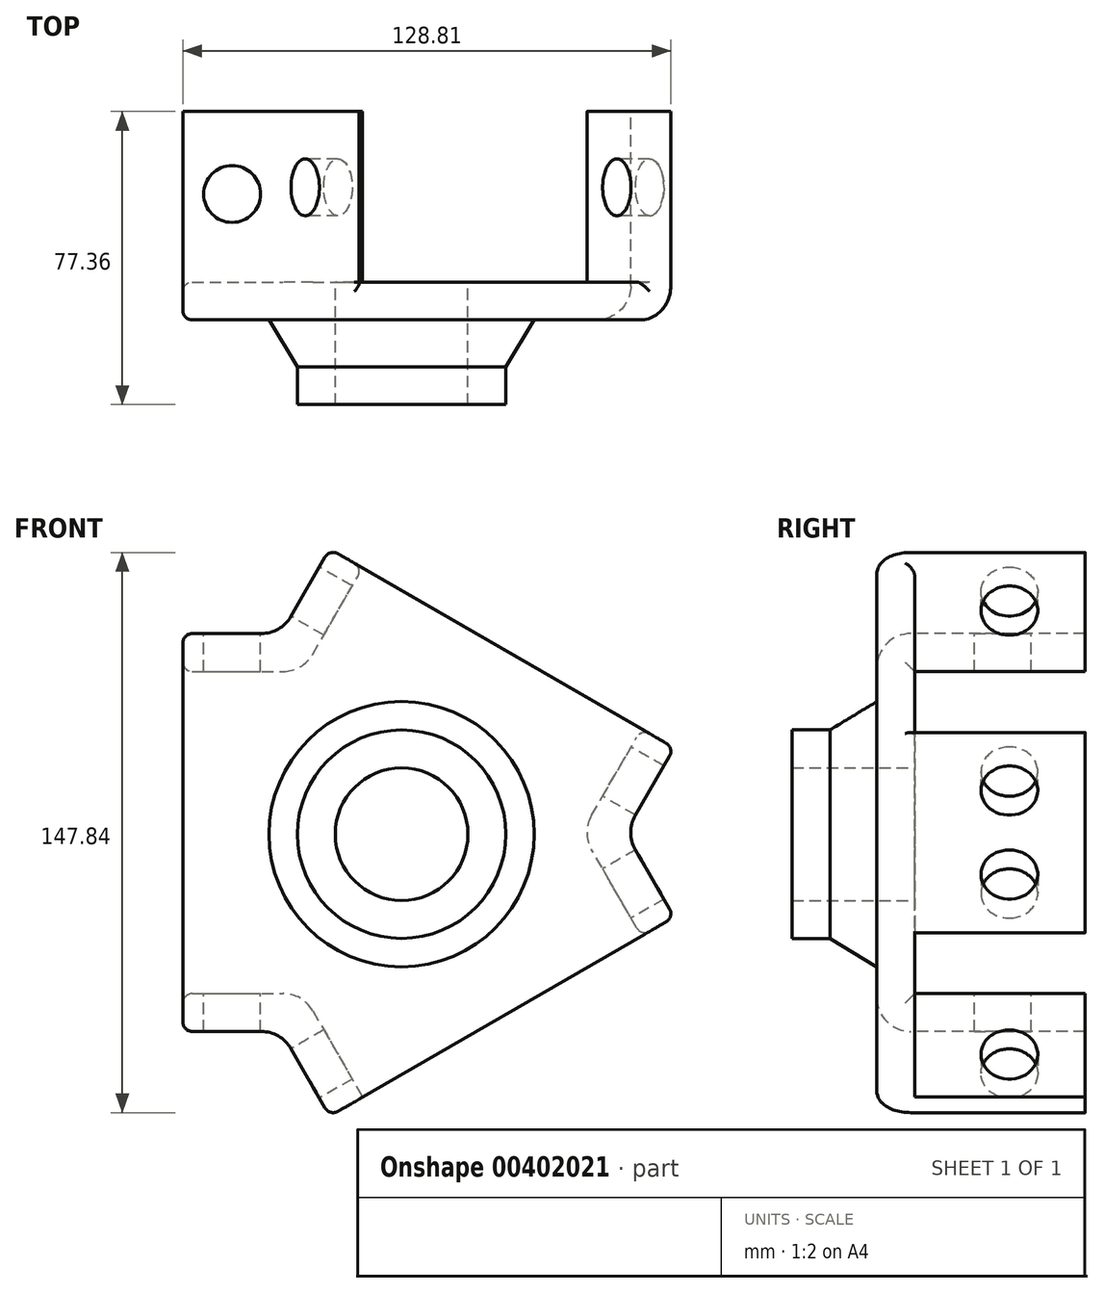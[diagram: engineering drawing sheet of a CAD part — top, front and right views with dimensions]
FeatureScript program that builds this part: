
annotation { "Feature Type Name" : "Feature", "Feature Type Description" : "" }
export const myFeature = defineFeature(function(context is Context, id is Id, definition is map)
    precondition{}
    {
        {
            var Q0;
            Q0=qCreatedBy(makeId("Front.planeOp"),FACE);
            var sketch = newSketch(context, id + "F0", { "sketchPlane" : qUnion([Q0])});
            skLineSegment(sketch, "E0", {"start": v(-84.9, 78.92) * mm, "end": v(-84.9, -26.08) * mm});
            skLineSegment(sketch, "E1", {"start": v(-84.9, 78.92) * mm, "end": v(-59, 78.92) * mm});
            skLineSegment(sketch, "E2", {"start": v(-59, 78.92) * mm, "end": v(-46.11, 101.26) * mm});
            skLineSegment(sketch, "E3", {"start": v(-46.11, 101.26) * mm, "end": v(44.82, 48.76) * mm});
            skLineSegment(sketch, "E4", {"start": v(44.82, 48.76) * mm, "end": v(31.92, 26.42) * mm});
            skLineSegment(sketch, "E5", {"start": v(31.92, 26.42) * mm, "end": v(44.82, 4.09) * mm});
            skLineSegment(sketch, "E6", {"start": v(44.82, 4.09) * mm, "end": v(-46.11, -48.41) * mm});
            skLineSegment(sketch, "E7", {"start": v(-46.11, -48.41) * mm, "end": v(-59, -26.08) * mm});
            skLineSegment(sketch, "E8", {"start": v(-84.9, -26.08) * mm, "end": v(-59, -26.08) * mm});
            skSolve(sketch);
        }
        {
            var Q0;
            Q0=makeQuery(id+"F0.imprint","IMPRINT",FACE,{"disambiguationData":[TD([[makeQuery(id+"F0.imprint","IMPRINT",EDGE,{"derivedFrom":sQuery(id+"F0.wireOp",EDGE,"E0")}),1.0]])]});
            extrude(context, id + "F1", {"entities" : qUnion([Q0]), "oppositeDirection" : true, "depth" : 10 * mm});
        }
        {
            var Q0;
            Q0=makeQuery(id+"F1.opExtrude","CAP_FACE",FACE,{"disambiguationData":[OSD([sQuery(id+"F0.wireOp",EDGE,"E0"),sQuery(id+"F0.wireOp",EDGE,"E1"),sQuery(id+"F0.wireOp",EDGE,"E2"),sQuery(id+"F0.wireOp",EDGE,"E3"),sQuery(id+"F0.wireOp",EDGE,"E4"),sQuery(id+"F0.wireOp",EDGE,"E5"),sQuery(id+"F0.wireOp",EDGE,"E6"),sQuery(id+"F0.wireOp",EDGE,"E7"),sQuery(id+"F0.wireOp",EDGE,"E8")])],"isStart":true});
            var sketch = newSketch(context, id + "F2", { "sketchPlane" : qUnion([Q0])});
            skPoint(sketch, "E9.startSnap0", {"position": v(-0.65, 75) * mm});
            skPoint(sketch, "E10", {"position": v(-27.16, 25.99) * mm});
            skSolve(sketch);
        }
        {
            var Q0;
            Q0=sQuery(id+"F2.wireOp",VERTEX,"E10");
            var Q1;
            Q1=sQuery(id+"F0.wireOp",EDGE,"E6");
            cPlane(context, id + "F3", {"entities" : qUnion([Q0, Q1]), "cplaneType" : CPlaneType.LINE_POINT, "offset" : 25 * mm, "width" : 150 * mm, "height" : 150 * mm});
        }
        {
            var Q0;
            Q0=qCreatedBy(id+"F3.planeOp",FACE);
            var sketch = newSketch(context, id + "F4", { "sketchPlane" : qUnion([Q0])});
            skLineSegment(sketch, "E11", {"start": v(0, 36.09) * mm, "end": v(78.9, 36.09) * mm, "construction": true});
            skLineSegment(sketch, "E12", {"start": v(22.36, 18.59) * mm, "end": v(12.36, 18.59) * mm});
            skLineSegment(sketch, "E13", {"start": v(12.36, 18.59) * mm, "end": v(12.36, 8.59) * mm});
            skLineSegment(sketch, "E14", {"start": v(12.36, 8.59) * mm, "end": v(22.36, 8.59) * mm});
            skLineSegment(sketch, "E15", {"start": v(22.36, 8.59) * mm, "end": v(22.36, 18.59) * mm});
            skLineSegment(sketch, "E16", {"start": v(0, 36.09) * mm, "end": v(0, 1.09) * mm});
            skLineSegment(sketch, "E17", {"start": v(12.36, 8.59) * mm, "end": v(0, 1.09) * mm});
            skLineSegment(sketch, "E18", {"start": v(12.36, 18.59) * mm, "end": v(-0.14, 18.59) * mm});
            skSolve(sketch);
        }
        {
            var Q0;
            Q0=makeQuery(id+"F1.opExtrude","CAP_FACE",FACE,{"disambiguationData":[OSD([sQuery(id+"F0.wireOp",EDGE,"E0"),sQuery(id+"F0.wireOp",EDGE,"E1"),sQuery(id+"F0.wireOp",EDGE,"E2"),sQuery(id+"F0.wireOp",EDGE,"E3"),sQuery(id+"F0.wireOp",EDGE,"E4"),sQuery(id+"F0.wireOp",EDGE,"E5"),sQuery(id+"F0.wireOp",EDGE,"E6"),sQuery(id+"F0.wireOp",EDGE,"E7"),sQuery(id+"F0.wireOp",EDGE,"E8")])],"isStart":false});
            var sketch = newSketch(context, id + "F5", { "sketchPlane" : qUnion([Q0])});
            skLineSegment(sketch, "E19.0", {"start": v(46.11, -48.41) * mm, "end": v(59, -26.08) * mm});
            skLineSegment(sketch, "E20.0", {"start": v(84.9, -26.08) * mm, "end": v(59, -26.08) * mm});
            skLineSegment(sketch, "E21.0", {"start": v(84.9, 78.92) * mm, "end": v(59, 78.92) * mm});
            skLineSegment(sketch, "E22.0", {"start": v(59, 78.92) * mm, "end": v(46.11, 101.26) * mm});
            skLineSegment(sketch, "E23.0", {"start": v(-31.92, 26.42) * mm, "end": v(-44.82, 4.09) * mm});
            skLineSegment(sketch, "E24.0", {"start": v(-44.82, 48.76) * mm, "end": v(-31.92, 26.42) * mm});
            skLineSegment(sketch, "E25", {"start": v(84.9, -26.08) * mm, "end": v(84.9, -16.08) * mm});
            skLineSegment(sketch, "E26", {"start": v(84.9, -16.08) * mm, "end": v(53.24, -16.08) * mm});
            skLineSegment(sketch, "E27", {"start": v(53.24, -16.08) * mm, "end": v(37.45, -43.41) * mm});
            skLineSegment(sketch, "E28", {"start": v(-36.16, -0.91) * mm, "end": v(-20.38, 26.42) * mm});
            skLineSegment(sketch, "E29", {"start": v(-20.38, 26.42) * mm, "end": v(-36.16, 53.76) * mm});
            skLineSegment(sketch, "E30", {"start": v(84.9, 68.92) * mm, "end": v(53.24, 68.92) * mm});
            skLineSegment(sketch, "E31", {"start": v(53.24, 68.92) * mm, "end": v(37.45, 96.26) * mm});
            skSolve(sketch);
        }
        {
            var Q0;
            {var subQ0=sQuery(id+"F5.wireOp",EDGE,"E19.0");Q0=makeQuery(id+"F5.imprint","IMPRINT",FACE,{"disambiguationData":[TD([[makeQuery(id+"F5.imprint","IMPRINT",EDGE,{"derivedFrom":subQ0}),1.0]])]});}
            var Q1;
            {var subQ4=sQuery(id+"F5.wireOp",EDGE,"E23.0");Q1=makeQuery(id+"F5.imprint","IMPRINT",FACE,{"disambiguationData":[TD([[makeQuery(id+"F5.imprint","IMPRINT",EDGE,{"derivedFrom":subQ4}),1.0]])]});}
            var Q2;
            {var subQ3=sQuery(id+"F5.wireOp",EDGE,"E21.0");Q2=makeQuery(id+"F5.imprint","IMPRINT",FACE,{"disambiguationData":[TD([[makeQuery(id+"F5.imprint","IMPRINT",EDGE,{"derivedFrom":subQ3}),1.0]])]});}
            extrude(context, id + "F6", {"entities" : qUnion([Q0, Q1, Q2]), "operationType" : NewBodyOperationType.ADD, "depth" : 45 * mm});
        }
        {
            var Q0;
            Q0=makeQuery(id+"F4.imprint","IMPRINT",FACE,{"disambiguationData":[TD([[makeQuery(id+"F4.imprint","IMPRINT",EDGE,{"derivedFrom":sQuery(id+"F4.wireOp",EDGE,"E12")}),1.0]])]});
            var Q1;
            {var subQ0=sQuery(id+"F4.wireOp",EDGE,"E13");Q1=makeQuery(id+"F4.imprint","IMPRINT",FACE,{"disambiguationData":[TD([[makeQuery(id+"F4.imprint","IMPRINT",EDGE,{"derivedFrom":subQ0}),-1.0]])]});}
            var Q2;
            Q2=sQuery(id+"F4.wireOp",EDGE,"E11");
            revolve(context, id + "F7", {"operationType" : NewBodyOperationType.ADD, "entities" : qUnion([Q0, Q1]), "axis" : qUnion([Q2]), "revolveType" : RevolveType.FULL});
        }
        {
            var Q0;
            Q0=makeQuery(id+"F6.boolean.opBoolean","MERGE",FACE,{"derivedFrom":[makeQuery(id+"F1.opExtrude","SWEPT_FACE",FACE,{"disambiguationData":[OSD([sQuery(id+"F0.wireOp",EDGE,"E2")])]}),makeQuery(id+"F6.opExtrude","SWEPT_FACE",FACE,{"disambiguationData":[OSD([sQuery(id+"F5.wireOp",EDGE,"E22.0")])]})]});
            var sketch = newSketch(context, id + "F8", { "sketchPlane" : qUnion([Q0])});
            skCircle(sketch, "E32", {"center": v(-35, 51.63) * mm, "radius": 7.5 * mm});
            skSolve(sketch);
        }
        {
            var Q0;
            Q0=makeQuery(id+"F6.boolean.opBoolean","MERGE",FACE,{"derivedFrom":[makeQuery(id+"F1.opExtrude","SWEPT_FACE",FACE,{"disambiguationData":[OSD([sQuery(id+"F0.wireOp",EDGE,"E1")])]}),makeQuery(id+"F6.opExtrude","SWEPT_FACE",FACE,{"disambiguationData":[OSD([sQuery(id+"F5.wireOp",EDGE,"E21.0")])]})]});
            var sketch = newSketch(context, id + "F9", { "sketchPlane" : qUnion([Q0])});
            skCircle(sketch, "E33", {"center": v(-71.9, 33.23) * mm, "radius": 7.5 * mm});
            skSolve(sketch);
        }
        {
            var Q0;
            Q0=makeQuery(id+"F6.boolean.opBoolean","MERGE",FACE,{"derivedFrom":[makeQuery(id+"F1.opExtrude","SWEPT_FACE",FACE,{"disambiguationData":[OSD([sQuery(id+"F0.wireOp",EDGE,"E7")])]}),makeQuery(id+"F6.opExtrude","SWEPT_FACE",FACE,{"disambiguationData":[OSD([sQuery(id+"F5.wireOp",EDGE,"E19.0")])]})]});
            var sketch = newSketch(context, id + "F10", { "sketchPlane" : qUnion([Q0])});
            skCircle(sketch, "E34", {"center": v(-35, -5.87) * mm, "radius": 7.5 * mm});
            skSolve(sketch);
        }
        {
            var Q0;
            Q0=makeQuery(id+"F8.imprint","IMPRINT",FACE,{"disambiguationData":[TD([[makeQuery(id+"F8.imprint","IMPRINT",EDGE,{"derivedFrom":sQuery(id+"F8.wireOp",EDGE,"E32")}),1.0]])]});
            extrude(context, id + "F11", {"entities" : qUnion([Q0]), "operationType" : NewBodyOperationType.REMOVE, "oppositeDirection" : true, "depth" : 150 * mm});
        }
        {
            var Q0;
            Q0=makeQuery(id+"F10.imprint","IMPRINT",FACE,{"disambiguationData":[TD([[makeQuery(id+"F10.imprint","IMPRINT",EDGE,{"derivedFrom":sQuery(id+"F10.wireOp",EDGE,"E34")}),1.0]])]});
            extrude(context, id + "F12", {"entities" : qUnion([Q0]), "operationType" : NewBodyOperationType.REMOVE, "oppositeDirection" : true, "depth" : 120 * mm});
        }
        {
            var Q0;
            Q0=makeQuery(id+"F9.imprint","IMPRINT",FACE,{"disambiguationData":[TD([[makeQuery(id+"F9.imprint","IMPRINT",EDGE,{"derivedFrom":sQuery(id+"F9.wireOp",EDGE,"E33")}),1.0]])]});
            extrude(context, id + "F13", {"entities" : qUnion([Q0]), "operationType" : NewBodyOperationType.REMOVE, "oppositeDirection" : true, "depth" : 120 * mm});
        }
        {
            var Q0;
            Q0=makeQuery(id+"F1.opExtrude","CAP_EDGE",EDGE,{"disambiguationData":[OSD([sQuery(id+"F0.wireOp",EDGE,"E8")])],"isStart":true});
            var Q1;
            Q1=makeQuery(id+"F1.opExtrude","CAP_EDGE",EDGE,{"disambiguationData":[OSD([sQuery(id+"F0.wireOp",EDGE,"E7")])],"isStart":true});
            var Q2;
            Q2=makeQuery(id+"F6.boolean.opBoolean","MERGE",EDGE,{"derivedFrom":[makeQuery(id+"F1.opExtrude","SWEPT_EDGE",EDGE,{"disambiguationData":[OSD([sQuery(id+"F0.wireOp",EDGE,"E7"),sQuery(id+"F0.wireOp",EDGE,"E8")])]}),makeQuery(id+"F6.opExtrude","SWEPT_EDGE",EDGE,{"disambiguationData":[OSD([sQuery(id+"F5.wireOp",EDGE,"E19.0"),sQuery(id+"F5.wireOp",EDGE,"E20.0")])]})]});
            var Q3;
            Q3=makeQuery(id+"F1.opExtrude","CAP_EDGE",EDGE,{"disambiguationData":[OSD([sQuery(id+"F0.wireOp",EDGE,"E2")])],"isStart":true});
            var Q4;
            Q4=makeQuery(id+"F1.opExtrude","CAP_EDGE",EDGE,{"disambiguationData":[OSD([sQuery(id+"F0.wireOp",EDGE,"E1")])],"isStart":true});
            var Q5;
            Q5=makeQuery(id+"F6.boolean.opBoolean","MERGE",EDGE,{"derivedFrom":[makeQuery(id+"F1.opExtrude","SWEPT_EDGE",EDGE,{"disambiguationData":[OSD([sQuery(id+"F0.wireOp",EDGE,"E1"),sQuery(id+"F0.wireOp",EDGE,"E2")])]}),makeQuery(id+"F6.opExtrude","SWEPT_EDGE",EDGE,{"disambiguationData":[OSD([sQuery(id+"F5.wireOp",EDGE,"E21.0"),sQuery(id+"F5.wireOp",EDGE,"E22.0")])]})]});
            var Q6;
            Q6=makeQuery(id+"F1.opExtrude","CAP_EDGE",EDGE,{"disambiguationData":[OSD([sQuery(id+"F0.wireOp",EDGE,"E5")])],"isStart":true});
            var Q7;
            Q7=makeQuery(id+"F1.opExtrude","CAP_EDGE",EDGE,{"disambiguationData":[OSD([sQuery(id+"F0.wireOp",EDGE,"E4")])],"isStart":true});
            var Q8;
            Q8=makeQuery(id+"F6.boolean.opBoolean","MERGE",EDGE,{"derivedFrom":[makeQuery(id+"F1.opExtrude","SWEPT_EDGE",EDGE,{"disambiguationData":[OSD([sQuery(id+"F0.wireOp",EDGE,"E4"),sQuery(id+"F0.wireOp",EDGE,"E5")])]}),makeQuery(id+"F6.opExtrude","SWEPT_EDGE",EDGE,{"disambiguationData":[OSD([sQuery(id+"F5.wireOp",EDGE,"E23.0"),sQuery(id+"F5.wireOp",EDGE,"E24.0")])]})]});
            var Q9;
            Q9=makeQuery(id+"F6.opExtrude","CAP_EDGE",EDGE,{"disambiguationData":[OSD([sQuery(id+"F5.wireOp",EDGE,"E31")])],"isStart":true});
            var Q10;
            Q10=makeQuery(id+"F6.opExtrude","CAP_EDGE",EDGE,{"disambiguationData":[OSD([sQuery(id+"F5.wireOp",EDGE,"E30")])],"isStart":true});
            var Q11;
            Q11=makeQuery(id+"F6.opExtrude","SWEPT_EDGE",EDGE,{"disambiguationData":[OSD([sQuery(id+"F5.wireOp",EDGE,"E30"),sQuery(id+"F5.wireOp",EDGE,"E31")])]});
            var Q12;
            Q12=makeQuery(id+"F6.opExtrude","CAP_EDGE",EDGE,{"disambiguationData":[OSD([sQuery(id+"F5.wireOp",EDGE,"E27")])],"isStart":true});
            var Q13;
            Q13=makeQuery(id+"F6.opExtrude","CAP_EDGE",EDGE,{"disambiguationData":[OSD([sQuery(id+"F5.wireOp",EDGE,"E26")])],"isStart":true});
            var Q14;
            Q14=makeQuery(id+"F6.opExtrude","SWEPT_EDGE",EDGE,{"disambiguationData":[OSD([sQuery(id+"F5.wireOp",EDGE,"E26"),sQuery(id+"F5.wireOp",EDGE,"E27")])]});
            var Q15;
            Q15=makeQuery(id+"F6.opExtrude","SWEPT_EDGE",EDGE,{"disambiguationData":[OSD([sQuery(id+"F5.wireOp",EDGE,"E28"),sQuery(id+"F5.wireOp",EDGE,"E29")])]});
            var Q16;
            Q16=makeQuery(id+"F6.opExtrude","CAP_EDGE",EDGE,{"disambiguationData":[OSD([sQuery(id+"F5.wireOp",EDGE,"E28")])],"isStart":true});
            var Q17;
            Q17=makeQuery(id+"F6.opExtrude","CAP_EDGE",EDGE,{"disambiguationData":[OSD([sQuery(id+"F5.wireOp",EDGE,"E29")])],"isStart":true});
            fillet(context, id + "F14", {"entities" : qUnion([Q0, Q1, Q2, Q3, Q4, Q5, Q6, Q7, Q8, Q9, Q10, Q11, Q12, Q13, Q14, Q15, Q16, Q17]), "radius" : 9 * mm, "allowEdgeOverflow" : false});
        }
        {
            var Q0;
            Q0=makeQuery(id+"F1.opExtrude","CAP_EDGE",EDGE,{"disambiguationData":[OSD([sQuery(id+"F0.wireOp",EDGE,"E0")])],"isStart":true});
            var Q1;
            Q1=makeQuery(id+"F1.opExtrude","CAP_EDGE",EDGE,{"disambiguationData":[OSD([sQuery(id+"F0.wireOp",EDGE,"E0")])],"isStart":false});
            var Q2;
            Q2=makeQuery(id+"F6.opExtrude","SWEPT_EDGE",EDGE,{"disambiguationData":[OSD([sQuery(id+"F0.wireOp",EDGE,"E0"),sQuery(id+"F5.wireOp",EDGE,"E30")])]});
            var Q3;
            Q3=makeQuery(id+"F6.opExtrude","SWEPT_EDGE",EDGE,{"disambiguationData":[OSD([sQuery(id+"F0.wireOp",EDGE,"E0"),sQuery(id+"F5.wireOp",EDGE,"E25"),sQuery(id+"F5.wireOp",EDGE,"E26")])]});
            var Q4;
            {var subQ0=sQuery(id+"F0.wireOp",EDGE,"E3");Q4=makeQuery(id+"F6.boolean.opBoolean","MERGE",EDGE,{"derivedFrom":[makeQuery(id+"F1.opExtrude","SWEPT_EDGE",EDGE,{"disambiguationData":[OSD([sQuery(id+"F0.wireOp",EDGE,"E2"),subQ0])]}),makeQuery(id+"F6.opExtrude","SWEPT_EDGE",EDGE,{"disambiguationData":[OSD([subQ0,sQuery(id+"F5.wireOp",EDGE,"E22.0")])]})]});}
            var Q5;
            Q5=makeQuery(id+"F6.opExtrude","SWEPT_EDGE",EDGE,{"disambiguationData":[OSD([sQuery(id+"F0.wireOp",EDGE,"E3"),sQuery(id+"F5.wireOp",EDGE,"E31")])]});
            var Q6;
            Q6=makeQuery(id+"F1.opExtrude","CAP_EDGE",EDGE,{"disambiguationData":[OSD([sQuery(id+"F0.wireOp",EDGE,"E3")])],"isStart":false});
            var Q7;
            Q7=makeQuery(id+"F6.opExtrude","SWEPT_EDGE",EDGE,{"disambiguationData":[OSD([sQuery(id+"F0.wireOp",EDGE,"E3"),sQuery(id+"F5.wireOp",EDGE,"E29")])]});
            var Q8;
            {var subQ0=sQuery(id+"F0.wireOp",EDGE,"E6");Q8=makeQuery(id+"F6.boolean.opBoolean","MERGE",EDGE,{"derivedFrom":[makeQuery(id+"F1.opExtrude","SWEPT_EDGE",EDGE,{"disambiguationData":[OSD([sQuery(id+"F0.wireOp",EDGE,"E5"),subQ0])]}),makeQuery(id+"F6.opExtrude","SWEPT_EDGE",EDGE,{"disambiguationData":[OSD([subQ0,sQuery(id+"F5.wireOp",EDGE,"E23.0")])]})]});}
            var Q9;
            Q9=makeQuery(id+"F6.opExtrude","SWEPT_EDGE",EDGE,{"disambiguationData":[OSD([sQuery(id+"F0.wireOp",EDGE,"E6"),sQuery(id+"F5.wireOp",EDGE,"E28")])]});
            fillet(context, id + "F15", {"entities" : qUnion([Q0, Q1, Q2, Q3, Q4, Q5, Q6, Q7, Q8, Q9]), "radius" : 2.5 * mm, "tangentPropagation" : true, "allowEdgeOverflow" : false});
        }
        {
            var Q0;
            Q0=makeQuery(id+"F7.boolean.opBoolean","SPLIT",FACE,{"disambiguationData":[TD([makeQuery(id+"F7.opRevolve","SWEPT_FACE",FACE,{"disambiguationData":[OSD([sQuery(id+"F4.wireOp",EDGE,"E12"),sQuery(id+"F4.wireOp",EDGE,"E18")])]})])],"derivedFrom":makeQuery(id+"F1.opExtrude","CAP_FACE",FACE,{"disambiguationData":[OSD([sQuery(id+"F0.wireOp",EDGE,"E0"),sQuery(id+"F0.wireOp",EDGE,"E1"),sQuery(id+"F0.wireOp",EDGE,"E2"),sQuery(id+"F0.wireOp",EDGE,"E3"),sQuery(id+"F0.wireOp",EDGE,"E4"),sQuery(id+"F0.wireOp",EDGE,"E5"),sQuery(id+"F0.wireOp",EDGE,"E6"),sQuery(id+"F0.wireOp",EDGE,"E7"),sQuery(id+"F0.wireOp",EDGE,"E8")])],"isStart":true})});
            extrude(context, id + "F16", {"entities" : qUnion([Q0]), "operationType" : NewBodyOperationType.REMOVE, "oppositeDirection" : true, "depth" : 25 * mm});
        }
    });
